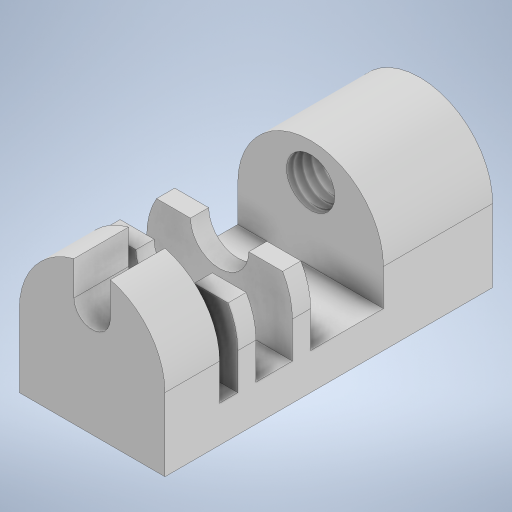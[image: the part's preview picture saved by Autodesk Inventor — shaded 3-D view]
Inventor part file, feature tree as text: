
AUTODESK INVENTOR PART (.ipt)
format: ipt  version: 2023 (Build 270158030, 158C)  size: 311,296 bytes
history: native  units: mm
features: sketch x7, extrude x6, fillet x1, hole x1
ambient origin geometry x8: Origin, YZ Plane, XZ Plane, XY Plane, X Axis, Y Axis, Z Axis, Center Point
bodies: Solid1 (feature_tree)
feature tree (15):
  extrude  "Extrusion1"  Depth=20.0mm
  fillet  "Fillet1"  Radius=45.0mm
  extrude  "Extrusion2"  Depth=15.0mm
  extrude  "Extrusion3"  Depth=27.5mm
  hole  "Hole1"  [1 undecoded]
  extrude  "Extrusion4"  Depth=5.0mm
  extrude  "Extrusion5"  Depth=45.0mm TaperAngle=0.0deg
  extrude  "Extrusion6"  Depth=10.0mm
  sketch  "Sketch1"  dims[d0=20.0mm d1=20.0mm d2=45.0mm d3=0.0mm]
  sketch  "Sketch2"  dims[d4=10.0mm d5=15.0mm]
  sketch  "Sketch3"  dims[d6=25.0mm d7=27.5mm]
  sketch  "Sketch4"  dims[d8=32.5mm d9=35.0mm]
  sketch  "Sketch5"  dims[d10=37.5mm d11=5.0mm]
  sketch  "Sketch6"  dims[d12=21.0mm d13=45.0mm d14=0.0mm]
  sketch  "Sketch7"  dims[d15=15.0mm d16=6.0mm d17=0.5mm d18=0.5mm d19=45.0mm d20=0.0mm d21=4.0mm d22=15.0mm d23=6.647mm d24=16.0mm d25=4.0mm d26=2.0mm d27=90.0deg d28=8.0mm d29=0.0mm d31=5.0mm d32=2.5mm d33=2.5mm d34=6.0mm d35=45.0mm d36=0.0mm d37=8.0mm d38=10.0mm d39=0.0mm d40=5.0mm d41=7.5mm d42=10.0mm d43=0.0mm]
note: 1 required parameter value undecoded (feature->parameter linkage not recoverable at this tier; creation-order binding heuristic only, values carry confidence <= 0.55)
